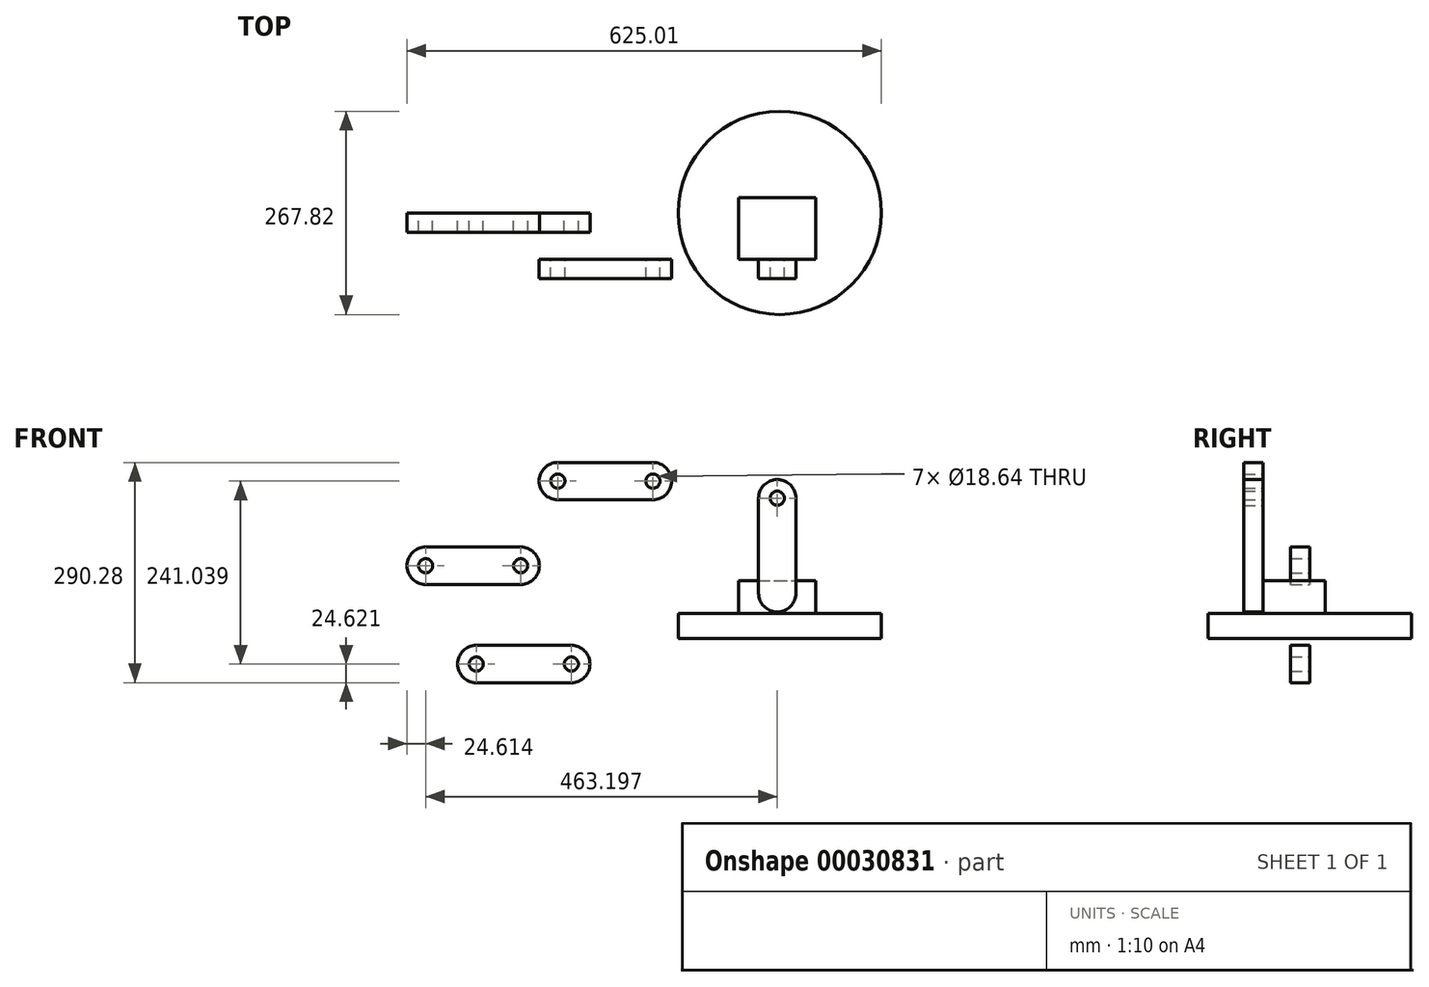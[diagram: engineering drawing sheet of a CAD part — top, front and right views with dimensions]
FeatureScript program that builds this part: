
annotation { "Feature Type Name" : "Feature", "Feature Type Description" : "" }
export const myFeature = defineFeature(function(context is Context, id is Id, definition is map)
    precondition{}
    {
        {
            var Q0;
            Q0=qCreatedBy(makeId("Front.planeOp"),FACE);
            var sketch = newSketch(context, id + "F0", { "sketchPlane" : qUnion([Q0])});
            skLineSegment(sketch, "E0.bottom", {"start": v(-399.79, -9.1) * mm, "end": v(-274.6, -9.1) * mm});
            skLineSegment(sketch, "E0.top", {"start": v(-399.79, -58.34) * mm, "end": v(-274.6, -58.34) * mm});
            skLineSegment(sketch, "E0.left", {"start": v(-399.79, -9.1) * mm, "end": v(-399.79, -58.34) * mm});
            skLineSegment(sketch, "E0.right", {"start": v(-274.6, -9.1) * mm, "end": v(-274.6, -58.34) * mm});
            skCircle(sketch, "E1", {"center": v(-274.6, -33.72) * mm, "radius": 24.62 * mm});
            skCircle(sketch, "E2", {"center": v(-399.79, -33.72) * mm, "radius": 24.62 * mm});
            skCircle(sketch, "E3", {"center": v(-274.6, -33.72) * mm, "radius": 9.32 * mm});
            skCircle(sketch, "E4", {"center": v(-399.79, -33.72) * mm, "radius": 9.32 * mm});
            skLineSegment(sketch, "E5.left", {"start": v(-466.49, 120.43) * mm, "end": v(-466.49, 71.2) * mm});
            skLineSegment(sketch, "E5.top", {"start": v(-466.49, 71.2) * mm, "end": v(-341.3, 71.2) * mm});
            skLineSegment(sketch, "E5.bottom", {"start": v(-466.49, 120.43) * mm, "end": v(-341.3, 120.43) * mm});
            skLineSegment(sketch, "E5.right", {"start": v(-341.3, 120.43) * mm, "end": v(-341.3, 71.2) * mm});
            skCircle(sketch, "E6", {"center": v(-341.3, 95.8) * mm, "radius": 24.62 * mm});
            skCircle(sketch, "E7", {"center": v(-466.49, 95.8) * mm, "radius": 24.62 * mm});
            skCircle(sketch, "E8", {"center": v(-341.3, 95.8) * mm, "radius": 9.32 * mm});
            skCircle(sketch, "E9", {"center": v(-466.49, 95.8) * mm, "radius": 9.32 * mm});
            skSolve(sketch);
        }
        {
            var Q0;
            Q0 = qSketchRegion(id + "F0", true);
            extrude(context, id + "F1", {"entities" : qUnion([Q0]), "depth" : 25.4 * mm});
        }
        {
            var Q0;
            Q0=qCreatedBy(makeId("Top.planeOp"),FACE);
            var sketch = newSketch(context, id + "F2", { "sketchPlane" : qUnion([Q0])});
            skCircle(sketch, "E10", {"center": v(0, 0) * mm, "radius": 133.9 * mm});
            skSolve(sketch);
        }
        {
            var Q0;
            Q0 = qSketchRegion(id + "F2", true);
            extrude(context, id + "F3", {"entities" : qUnion([Q0]), "depth" : 32.88 * mm});
        }
        {
            var Q0;
            Q0=makeQuery(id+"F3.opExtrude","CAP_FACE",FACE,{"disambiguationData":[OSD([sQuery(id+"F2.wireOp",EDGE,"E10")])],"isStart":false});
            var sketch = newSketch(context, id + "F4", { "sketchPlane" : qUnion([Q0])});
            skLineSegment(sketch, "E11.bottom", {"start": v(-54.09, 20.19) * mm, "end": v(47.51, 20.19) * mm});
            skLineSegment(sketch, "E11.top", {"start": v(-54.09, -61.4) * mm, "end": v(47.51, -61.4) * mm});
            skLineSegment(sketch, "E11.left", {"start": v(-54.09, 20.19) * mm, "end": v(-54.09, -61.4) * mm});
            skLineSegment(sketch, "E11.right", {"start": v(47.51, 20.19) * mm, "end": v(47.51, -61.4) * mm});
            skSolve(sketch);
        }
        {
            var Q0;
            Q0 = qSketchRegion(id + "F4", true);
            extrude(context, id + "F5", {"entities" : qUnion([Q0]), "operationType" : NewBodyOperationType.ADD, "depth" : 43.1 * mm});
        }
        {
            var Q0;
            Q0=makeQuery(id+"F5.opExtrude","SWEPT_FACE",FACE,{"disambiguationData":[OSD([sQuery(id+"F4.wireOp",EDGE,"E11.top")])]});
            var sketch = newSketch(context, id + "F6", { "sketchPlane" : qUnion([Q0])});
            skCircle(sketch, "E12", {"center": v(-292.31, 207.32) * mm, "radius": 9.32 * mm});
            skLineSegment(sketch, "E13.bottom", {"start": v(-292.31, 231.94) * mm, "end": v(-167.13, 231.94) * mm});
            skLineSegment(sketch, "E13.top", {"start": v(-292.31, 182.7) * mm, "end": v(-167.13, 182.7) * mm});
            skLineSegment(sketch, "E13.left", {"start": v(-292.31, 231.94) * mm, "end": v(-292.31, 182.7) * mm});
            skLineSegment(sketch, "E13.right", {"start": v(-167.13, 231.94) * mm, "end": v(-167.13, 182.7) * mm});
            skCircle(sketch, "E14", {"center": v(-167.13, 207.32) * mm, "radius": 24.62 * mm});
            skCircle(sketch, "E15", {"center": v(-292.31, 207.32) * mm, "radius": 24.62 * mm});
            skCircle(sketch, "E16", {"center": v(-167.13, 207.32) * mm, "radius": 9.32 * mm});
            skLineSegment(sketch, "E17.bottom", {"start": v(-27.9, 59.66) * mm, "end": v(21.32, 59.66) * mm});
            skLineSegment(sketch, "E17.top", {"start": v(-27.9, 184.83) * mm, "end": v(21.32, 184.83) * mm});
            skLineSegment(sketch, "E17.left", {"start": v(-27.9, 59.66) * mm, "end": v(-27.9, 184.83) * mm});
            skLineSegment(sketch, "E17.right", {"start": v(21.32, 59.66) * mm, "end": v(21.32, 184.83) * mm});
            skCircle(sketch, "E18", {"center": v(-3.29, 184.83) * mm, "radius": 24.61 * mm});
            skCircle(sketch, "E19", {"center": v(-3.29, 59.66) * mm, "radius": 24.61 * mm});
            skCircle(sketch, "E20", {"center": v(-3.29, 184.83) * mm, "radius": 9.32 * mm});
            skCircle(sketch, "E21", {"center": v(-3.29, 59.66) * mm, "radius": 9.32 * mm});
            skSolve(sketch);
        }
        {
            var Q0;
            {var subQ1=sQuery(id+"F6.wireOp",EDGE,"E13.left");var subQ4=sQuery(id+"F6.wireOp",EDGE,"E12");var subQ6=makeQuery(id+"F6.imprint","INTERSECT",VERTEX,{"disambiguationData":[OD(0.0)],"derivedFrom":[subQ4,subQ1]});Q0=makeQuery(id+"F6.imprint","IMPRINT",FACE,{"disambiguationData":[TD([[makeQuery(id+"F6.imprint","IMPRINT",EDGE,{"disambiguationData":[TD([[subQ6,-1.0]])],"derivedFrom":subQ4}),-1.0]])]});}
            var Q1;
            {var subQ3=sQuery(id+"F6.wireOp",EDGE,"E13.bottom");Q1=makeQuery(id+"F6.imprint","IMPRINT",FACE,{"disambiguationData":[TD([[makeQuery(id+"F6.imprint","IMPRINT",EDGE,{"derivedFrom":subQ3}),-1.0]])]});}
            var Q2;
            {var subQ0=sQuery(id+"F6.wireOp",EDGE,"E16");var subQ1=sQuery(id+"F6.wireOp",EDGE,"E13.right");var subQ3=makeQuery(id+"F6.imprint","INTERSECT",VERTEX,{"disambiguationData":[OD(0.0)],"derivedFrom":[subQ1,subQ0]});Q2=makeQuery(id+"F6.imprint","IMPRINT",FACE,{"disambiguationData":[TD([[makeQuery(id+"F6.imprint","IMPRINT",EDGE,{"disambiguationData":[TD([[subQ3,1.0]])],"derivedFrom":subQ0}),-1.0]])]});}
            var Q3;
            {var subQ0=sQuery(id+"F6.wireOp",EDGE,"E20");var subQ1=sQuery(id+"F6.wireOp",EDGE,"E17.top");var subQ3=makeQuery(id+"F6.imprint","INTERSECT",VERTEX,{"disambiguationData":[OD(0.0)],"derivedFrom":[subQ1,subQ0]});Q3=makeQuery(id+"F6.imprint","IMPRINT",FACE,{"disambiguationData":[TD([[makeQuery(id+"F6.imprint","IMPRINT",EDGE,{"disambiguationData":[TD([[subQ3,1.0]])],"derivedFrom":subQ0}),-1.0]])]});}
            var Q4;
            {var subQ1=sQuery(id+"F6.wireOp",EDGE,"E13.left");var subQ4=sQuery(id+"F6.wireOp",EDGE,"E12");var subQ6=makeQuery(id+"F6.imprint","INTERSECT",VERTEX,{"disambiguationData":[OD(0.0)],"derivedFrom":[subQ4,subQ1]});Q4=makeQuery(id+"F6.imprint","IMPRINT",FACE,{"disambiguationData":[TD([[makeQuery(id+"F6.imprint","IMPRINT",EDGE,{"disambiguationData":[TD([[subQ6,1.0]])],"derivedFrom":subQ4}),-1.0]])]});}
            var Q5;
            {var subQ0=sQuery(id+"F6.wireOp",EDGE,"E16");var subQ1=sQuery(id+"F6.wireOp",EDGE,"E13.right");var subQ3=makeQuery(id+"F6.imprint","INTERSECT",VERTEX,{"disambiguationData":[OD(0.0)],"derivedFrom":[subQ1,subQ0]});Q5=makeQuery(id+"F6.imprint","IMPRINT",FACE,{"disambiguationData":[TD([[makeQuery(id+"F6.imprint","IMPRINT",EDGE,{"disambiguationData":[TD([[subQ3,-1.0]])],"derivedFrom":subQ0}),-1.0]])]});}
            var Q6;
            {var subQ0=sQuery(id+"F6.wireOp",EDGE,"E20");var subQ1=sQuery(id+"F6.wireOp",EDGE,"E17.top");var subQ3=makeQuery(id+"F6.imprint","INTERSECT",VERTEX,{"disambiguationData":[OD(0.0)],"derivedFrom":[subQ1,subQ0]});Q6=makeQuery(id+"F6.imprint","IMPRINT",FACE,{"disambiguationData":[TD([[makeQuery(id+"F6.imprint","IMPRINT",EDGE,{"disambiguationData":[TD([[subQ3,-1.0]])],"derivedFrom":subQ0}),-1.0]])]});}
            var Q7;
            {var subQ0=makeQuery(id+"F5.opExtrude","CAP_EDGE",EDGE,{"disambiguationData":[OSD([sQuery(id+"F4.wireOp",EDGE,"E11.top")])],"isStart":false});var subQ1=sQuery(id+"F6.wireOp",EDGE,"E19");var subQ3=makeQuery(id+"F6.imprint","INTERSECT",VERTEX,{"disambiguationData":[OD(0.0)],"derivedFrom":[subQ0,subQ1]});Q7=makeQuery(id+"F6.imprint","IMPRINT",FACE,{"disambiguationData":[TD([[makeQuery(id+"F6.imprint","IMPRINT",EDGE,{"disambiguationData":[TD([[subQ3,-1.0]])],"derivedFrom":subQ1}),1.0]])]});}
            var Q8;
            {var subQ1=makeQuery(id+"F5.opExtrude","CAP_EDGE",EDGE,{"disambiguationData":[OSD([sQuery(id+"F4.wireOp",EDGE,"E11.top")])],"isStart":false});var subQ3=sQuery(id+"F6.wireOp",EDGE,"E17.left");var subQ5=makeQuery(id+"F6.imprint","INTERSECT",VERTEX,{"derivedFrom":[subQ1,subQ3]});Q8=makeQuery(id+"F6.imprint","IMPRINT",FACE,{"disambiguationData":[TD([[makeQuery(id+"F6.imprint","IMPRINT",EDGE,{"disambiguationData":[TD([[subQ5,-1.0]])],"derivedFrom":subQ1}),-1.0]])]});}
            var Q9;
            {var subQ0=makeQuery(id+"F5.opExtrude","CAP_EDGE",EDGE,{"disambiguationData":[OSD([sQuery(id+"F4.wireOp",EDGE,"E11.top")])],"isStart":false});var subQ3=sQuery(id+"F6.wireOp",EDGE,"E17.right");var subQ4=makeQuery(id+"F6.imprint","INTERSECT",VERTEX,{"derivedFrom":[subQ0,subQ3]});Q9=makeQuery(id+"F6.imprint","IMPRINT",FACE,{"disambiguationData":[TD([[makeQuery(id+"F6.imprint","IMPRINT",EDGE,{"disambiguationData":[TD([[subQ4,1.0]])],"derivedFrom":subQ0}),-1.0]])]});}
            var Q10;
            {var subQ4=sQuery(id+"F6.wireOp",EDGE,"E21");var subQ5=sQuery(id+"F6.wireOp",EDGE,"E17.bottom");var subQ7=makeQuery(id+"F6.imprint","INTERSECT",VERTEX,{"disambiguationData":[OD(0.0)],"derivedFrom":[subQ5,subQ4]});Q10=makeQuery(id+"F6.imprint","IMPRINT",FACE,{"disambiguationData":[TD([[makeQuery(id+"F6.imprint","IMPRINT",EDGE,{"disambiguationData":[TD([[subQ7,1.0]])],"derivedFrom":subQ4}),-1.0]])]});}
            var Q11;
            {var subQ0=makeQuery(id+"F5.opExtrude","CAP_EDGE",EDGE,{"disambiguationData":[OSD([sQuery(id+"F4.wireOp",EDGE,"E11.top")])],"isStart":false});var subQ1=sQuery(id+"F6.wireOp",EDGE,"E19");var subQ2=makeQuery(id+"F6.imprint","INTERSECT",VERTEX,{"disambiguationData":[OD(0.0)],"derivedFrom":[subQ0,subQ1]});Q11=makeQuery(id+"F6.imprint","IMPRINT",FACE,{"disambiguationData":[TD([[makeQuery(id+"F6.imprint","IMPRINT",EDGE,{"disambiguationData":[TD([[subQ2,-1.0]])],"derivedFrom":subQ1}),-1.0]])]});}
            var Q12;
            {var subQ0=sQuery(id+"F6.wireOp",EDGE,"E21");var subQ1=sQuery(id+"F6.wireOp",EDGE,"E17.bottom");var subQ3=makeQuery(id+"F6.imprint","INTERSECT",VERTEX,{"disambiguationData":[OD(0.0)],"derivedFrom":[subQ1,subQ0]});Q12=makeQuery(id+"F6.imprint","IMPRINT",FACE,{"disambiguationData":[TD([[makeQuery(id+"F6.imprint","IMPRINT",EDGE,{"disambiguationData":[TD([[subQ3,-1.0]])],"derivedFrom":subQ0}),-1.0]])]});}
            var Q13;
            {var subQ0=sQuery(id+"F6.wireOp",EDGE,"E21");var subQ1=sQuery(id+"F6.wireOp",EDGE,"E17.bottom");var subQ3=makeQuery(id+"F6.imprint","INTERSECT",VERTEX,{"disambiguationData":[OD(0.0)],"derivedFrom":[subQ1,subQ0]});Q13=makeQuery(id+"F6.imprint","IMPRINT",FACE,{"disambiguationData":[TD([[makeQuery(id+"F6.imprint","IMPRINT",EDGE,{"disambiguationData":[TD([[subQ3,-1.0]])],"derivedFrom":subQ1}),1.0]])]});}
            var Q14;
            {var subQ0=sQuery(id+"F6.wireOp",EDGE,"E21");var subQ1=sQuery(id+"F6.wireOp",EDGE,"E17.bottom");var subQ3=makeQuery(id+"F6.imprint","INTERSECT",VERTEX,{"disambiguationData":[OD(0.0)],"derivedFrom":[subQ1,subQ0]});Q14=makeQuery(id+"F6.imprint","IMPRINT",FACE,{"disambiguationData":[TD([[makeQuery(id+"F6.imprint","IMPRINT",EDGE,{"disambiguationData":[TD([[subQ3,-1.0]])],"derivedFrom":subQ1}),-1.0]])]});}
            extrude(context, id + "F7", {"entities" : qUnion([Q0, Q1, Q2, Q3, Q4, Q5, Q6, Q7, Q8, Q9, Q10, Q11, Q12, Q13, Q14]), "operationType" : NewBodyOperationType.ADD, "depth" : 25.4 * mm});
        }
    });
